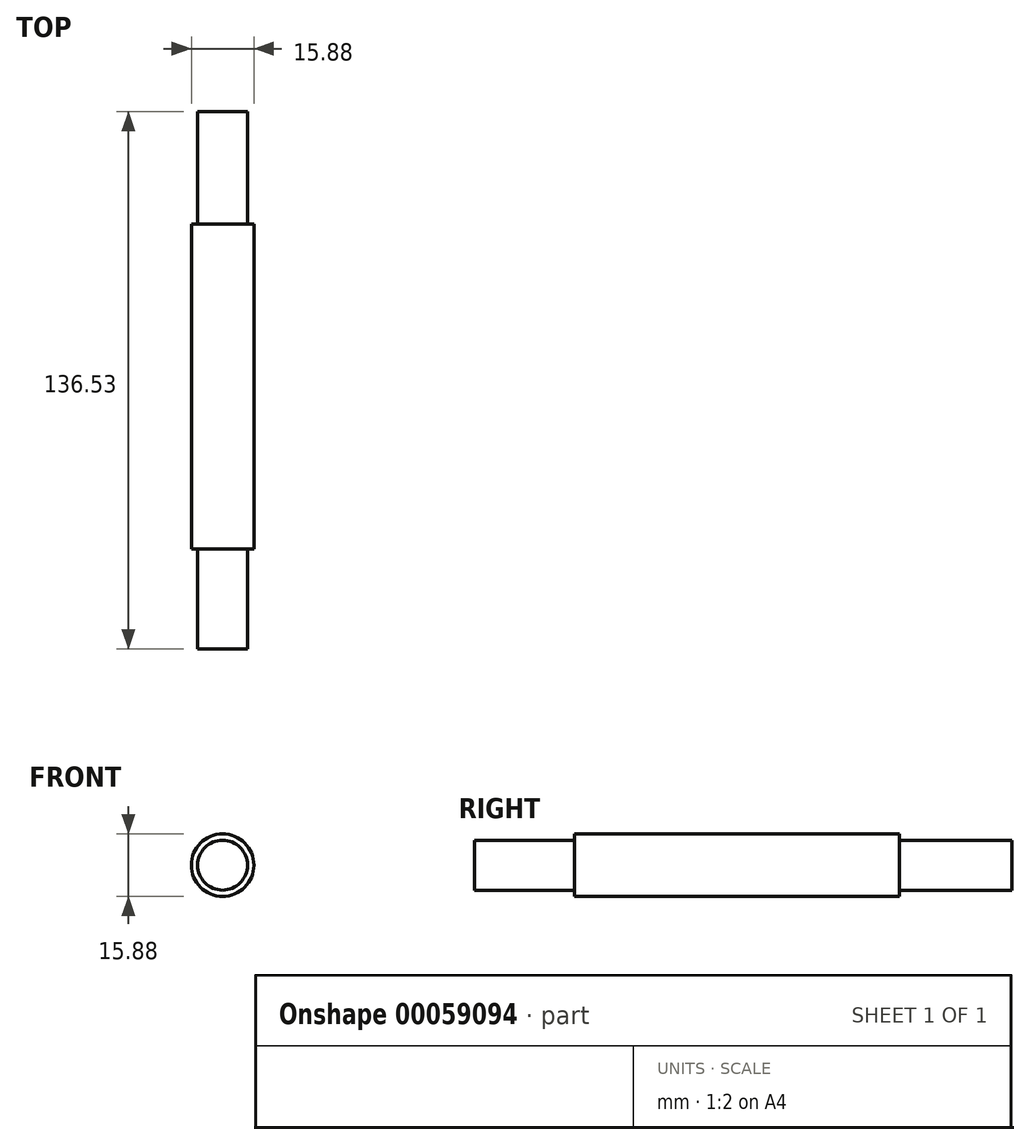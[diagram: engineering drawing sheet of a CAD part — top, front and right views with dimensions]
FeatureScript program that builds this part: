
annotation { "Feature Type Name" : "Feature", "Feature Type Description" : "" }
export const myFeature = defineFeature(function(context is Context, id is Id, definition is map)
    precondition{}
    {
        {
            var Q0;
            Q0=qCreatedBy(makeId("Front.planeOp"),FACE);
            var sketch = newSketch(context, id + "F0", { "sketchPlane" : qUnion([Q0])});
            skCircle(sketch, "E0", {"center": v(0, 0) * mm, "radius": 7.94 * mm});
            skSolve(sketch);
        }
        {
            var Q0;
            Q0=makeQuery(id+"F0.imprint","IMPRINT",FACE,{"disambiguationData":[TD([[makeQuery(id+"F0.imprint","IMPRINT",EDGE,{"derivedFrom":sQuery(id+"F0.wireOp",EDGE,"E0")}),1.0]])]});
            extrude(context, id + "F1", {"entities" : qUnion([Q0]), "depth" : 136.53 * mm});
        }
        {
            var Q0;
            Q0=makeQuery(id+"F1.opExtrude","CAP_FACE",FACE,{"disambiguationData":[OSD([sQuery(id+"F0.wireOp",EDGE,"E0")])],"isStart":false});
            var sketch = newSketch(context, id + "F2", { "sketchPlane" : qUnion([Q0])});
            skCircle(sketch, "E1", {"center": v(0, 0) * mm, "radius": 6.35 * mm});
            skCircle(sketch, "E2.0", {"center": v(0, 0) * mm, "radius": 7.94 * mm});
            skSolve(sketch);
        }
        {
            var Q0;
            Q0=makeQuery(id+"F2.imprint","IMPRINT",FACE,{"disambiguationData":[TD([[makeQuery(id+"F2.imprint","IMPRINT",EDGE,{"derivedFrom":sQuery(id+"F2.wireOp",EDGE,"E1")}),-1.0]])]});
            extrude(context, id + "F3", {"entities" : qUnion([Q0]), "operationType" : NewBodyOperationType.REMOVE, "oppositeDirection" : true, "depth" : 25.4 * mm});
        }
        {
            var Q0;
            Q0=makeQuery(id+"F1.opExtrude","CAP_FACE",FACE,{"disambiguationData":[OSD([sQuery(id+"F0.wireOp",EDGE,"E0")])],"isStart":true});
            var sketch = newSketch(context, id + "F4", { "sketchPlane" : qUnion([Q0])});
            skCircle(sketch, "E3", {"center": v(0, 0) * mm, "radius": 6.35 * mm});
            skCircle(sketch, "E4.0", {"center": v(0, 0) * mm, "radius": 7.94 * mm});
            skSolve(sketch);
        }
        {
            var Q0;
            Q0=makeQuery(id+"F4.imprint","IMPRINT",FACE,{"disambiguationData":[TD([[makeQuery(id+"F4.imprint","IMPRINT",EDGE,{"derivedFrom":sQuery(id+"F4.wireOp",EDGE,"E3")}),-1.0]])]});
            extrude(context, id + "F5", {"entities" : qUnion([Q0]), "operationType" : NewBodyOperationType.REMOVE, "oppositeDirection" : true, "depth" : 28.6 * mm});
        }
    });
